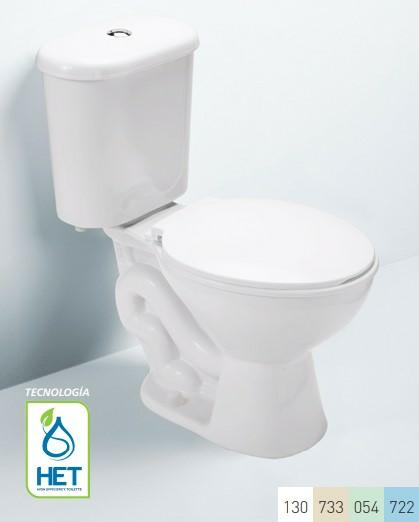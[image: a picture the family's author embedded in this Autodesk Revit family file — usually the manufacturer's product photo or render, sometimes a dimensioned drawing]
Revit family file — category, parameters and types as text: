
# Revit family: BRG-GRF-CCN_NIZA MONOMANDO PARA COCINA CROMO
name_source: partatom
category: Aparatos sanitarios
units: mm (PartAtom-declared; Revit-internal decimal feet)

## family parameters
Compartido = Sí
Corte con vacíos al cargar = No
Cota de conector redondo = Diámetro de uso
Número OmniClass = 23.45.00.00
Punto de cálculo de habitación = Sí
Se basa en plano de trabajo = No
Siempre vertical = Sí
Tipo de pieza = Normal
Título OmniClass = Sanitary, Laundry, and Cleaning Equipment

## types (1)
- NIZA MONOMANDO PARA COCINA
    Conexión AC = Sí
    Conexión AF = Sí
    Conexión de residuos = Sí
    Conexión de ventilación = Sí
    Fabricante = BRIGGSEcuador
    Imagen de tipo = <Ninguno>
    Modelo = NIZA MONOMANDO PARA COCINA
    URL = https://www.briggs.com.ec
    _ALT_Meson = 0.85 m
    _ALT_Toma = 0.55 m
    _EDESA_ Alto en cm = 25.5
    _EDESA_ Ancho en cm = 9
    _EDESA_ Categoría = Productos > Grifería > Cocina
    _EDESA_ Certificación = Cumple con norma NTE - INEN 3123 basada en la norma ASME 112.18.1 - 2012. Nuestras mangueras cuentan certificación cUPC.
    _EDESA_ Color = cromo
    _EDESA_ Conexión hidráulica = Entrada de agua: tubería ø 1/2" Salida de agua: tubería PVC 50
    _EDESA_ Consumo/capacidad de agua en L = 8.3 litros por minuto / 2.2 gpm a 60 psi
    _EDESA_ Descripción = Grifería monomando de cocina para agua fría y caliente. Instalación sobre fregadero o mesón. Incluye sifón y mangueras flexibles.
    _EDESA_ Garantía = De por vida para el cuerpo principal y acabado en cromo (306)
    _EDESA_ Marca = BRIGGS
    _EDESA_ Materiales = Latón
    _EDESA_ Nombre = NIZA MONOMANDO PARA COCINA
    _EDESA_ Productos incluídos = Sifón 1 1/2” PP con Acople, 2 Mangueras Monomando 16”
    _EDESA_ Productos necesarios para instalación = Desagüe para fregadero
    _EDESA_ Profundidad en cm = 22
    _EDESA_ Página web = https://www.briggs.com.ec
    _EDESA_ Sku/código = SG0063793061CW
    _EDESA_ Tipo de instalación = Sobre fregadero o mesón
